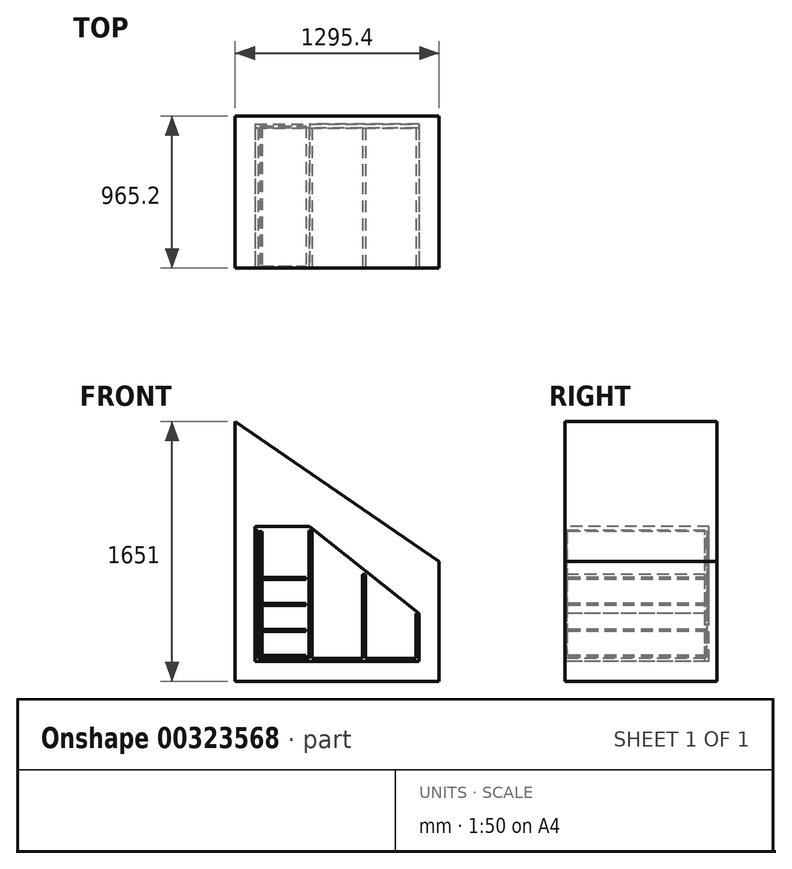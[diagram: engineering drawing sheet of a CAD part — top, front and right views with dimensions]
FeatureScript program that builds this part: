
annotation { "Feature Type Name" : "Feature", "Feature Type Description" : "" }
export const myFeature = defineFeature(function(context is Context, id is Id, definition is map)
    precondition{}
    {
        {
            var Q0;
            Q0=qCreatedBy(makeId("Front.planeOp"),FACE);
            var sketch = newSketch(context, id + "F0", { "sketchPlane" : qUnion([Q0])});
            skLineSegment(sketch, "E0", {"start": v(0, 0) * mm, "end": v(1295.4, 0) * mm});
            skLineSegment(sketch, "E1", {"start": v(1295.4, 0) * mm, "end": v(1295.4, 762) * mm});
            skLineSegment(sketch, "E2", {"start": v(1295.4, 762) * mm, "end": v(0, 1651) * mm});
            skLineSegment(sketch, "E3", {"start": v(0, 1651) * mm, "end": v(0, 0) * mm});
            skSolve(sketch);
        }
        {
            var Q0;
            Q0 = qSketchRegion(id + "F0", true);
            extrude(context, id + "F1", {"entities" : qUnion([Q0]), "depth" : 965.2 * mm});
        }
        {
            var Q0;
            Q0=makeQuery(id+"F1.opExtrude","CAP_FACE",FACE,{"disambiguationData":[OSD([sQuery(id+"F0.wireOp",EDGE,"E0"),sQuery(id+"F0.wireOp",EDGE,"E1"),sQuery(id+"F0.wireOp",EDGE,"E2"),sQuery(id+"F0.wireOp",EDGE,"E3")])],"isStart":false});
            var sketch = newSketch(context, id + "F2", { "sketchPlane" : qUnion([Q0])});
            skLineSegment(sketch, "E4", {"start": v(127, 127) * mm, "end": v(1168.4, 127) * mm});
            skLineSegment(sketch, "E5", {"start": v(1168.4, 127) * mm, "end": v(1168.4, 431.8) * mm});
            skLineSegment(sketch, "E6", {"start": v(1168.4, 431.8) * mm, "end": v(472.95, 985.52) * mm});
            skLineSegment(sketch, "E7", {"start": v(127, 127) * mm, "end": v(127, 985.52) * mm});
            skLineSegment(sketch, "E8", {"start": v(127, 985.52) * mm, "end": v(472.95, 985.52) * mm});
            skSolve(sketch);
        }
        {
            var Q0;
            Q0 = qSketchRegion(id + "F2", true);
            extrude(context, id + "F3", {"entities" : qUnion([Q0]), "operationType" : NewBodyOperationType.REMOVE, "oppositeDirection" : true, "depth" : 914.4 * mm});
        }
        {
            var Q0;
            Q0=makeQuery(id+"F1.opExtrude","CAP_FACE",FACE,{"disambiguationData":[OSD([sQuery(id+"F0.wireOp",EDGE,"E0"),sQuery(id+"F0.wireOp",EDGE,"E1"),sQuery(id+"F0.wireOp",EDGE,"E2"),sQuery(id+"F0.wireOp",EDGE,"E3")])],"isStart":false});
            var sketch = newSketch(context, id + "F4", { "sketchPlane" : qUnion([Q0])});
            skLineSegment(sketch, "E9", {"start": v(127, 127) * mm, "end": v(1168.4, 127) * mm});
            skLineSegment(sketch, "E10", {"start": v(1168.4, 127) * mm, "end": v(1168.4, 431.8) * mm});
            skLineSegment(sketch, "E11", {"start": v(1168.4, 431.8) * mm, "end": v(1149.35, 431.8) * mm});
            skLineSegment(sketch, "E12", {"start": v(1149.35, 431.8) * mm, "end": v(1149.35, 146.05) * mm});
            skLineSegment(sketch, "E13", {"start": v(1149.35, 146.05) * mm, "end": v(827.79, 146.05) * mm});
            skLineSegment(sketch, "E14", {"start": v(146.05, 146.05) * mm, "end": v(146.05, 958.85) * mm});
            skLineSegment(sketch, "E15", {"start": v(146.05, 958.85) * mm, "end": v(127, 958.85) * mm});
            skLineSegment(sketch, "E16", {"start": v(127, 958.85) * mm, "end": v(127, 127) * mm});
            skLineSegment(sketch, "E17.top", {"start": v(467.61, 958.85) * mm, "end": v(486.66, 958.85) * mm});
            skLineSegment(sketch, "E17.left", {"start": v(467.61, 146.05) * mm, "end": v(467.61, 958.85) * mm});
            skLineSegment(sketch, "E17.right", {"start": v(486.66, 146.05) * mm, "end": v(486.66, 958.85) * mm});
            skLineSegment(sketch, "E18.top", {"start": v(808.74, 679.45) * mm, "end": v(827.79, 679.45) * mm});
            skLineSegment(sketch, "E18.left", {"start": v(808.74, 146.05) * mm, "end": v(808.74, 679.45) * mm});
            skLineSegment(sketch, "E18.right", {"start": v(827.79, 146.05) * mm, "end": v(827.79, 679.45) * mm});
            skLineSegment(sketch, "E19.trimOffspring", {"start": v(467.61, 146.05) * mm, "end": v(146.05, 146.05) * mm});
            skLineSegment(sketch, "E20.trimOffspring", {"start": v(808.74, 146.05) * mm, "end": v(486.66, 146.05) * mm});
            skSolve(sketch);
        }
        {
            var Q0;
            Q0 = qSketchRegion(id + "F4", true);
            extrude(context, id + "F5", {"entities" : qUnion([Q0]), "oppositeDirection" : true, "depth" : 889 * mm});
        }
        {
            var Q0;
            Q0=makeQuery(id+"F1.opExtrude","CAP_FACE",FACE,{"disambiguationData":[OSD([sQuery(id+"F0.wireOp",EDGE,"E0"),sQuery(id+"F0.wireOp",EDGE,"E1"),sQuery(id+"F0.wireOp",EDGE,"E2"),sQuery(id+"F0.wireOp",EDGE,"E3")])],"isStart":false});
            cPlane(context, id + "F6", {"entities" : qUnion([Q0]), "cplaneType" : CPlaneType.OFFSET, "offset" : 12.7 * mm, "oppositeDirection" : true, "width" : 152.4 * mm, "height" : 152.4 * mm});
        }
        {
            var Q0;
            Q0=qCreatedBy(id+"F6.planeOp",FACE);
            var sketch = newSketch(context, id + "F7", { "sketchPlane" : qUnion([Q0])});
            skLineSegment(sketch, "E21", {"start": v(158.75, 152.4) * mm, "end": v(450.85, 152.4) * mm});
            skLineSegment(sketch, "E22", {"start": v(158.75, 152.4) * mm, "end": v(158.75, 952.5) * mm});
            skLineSegment(sketch, "E23", {"start": v(158.75, 952.5) * mm, "end": v(171.45, 952.5) * mm});
            skLineSegment(sketch, "E24", {"start": v(171.45, 952.5) * mm, "end": v(171.45, 660.4) * mm});
            skLineSegment(sketch, "E25", {"start": v(171.45, 165.1) * mm, "end": v(450.85, 165.1) * mm});
            skLineSegment(sketch, "E26", {"start": v(450.85, 152.4) * mm, "end": v(450.85, 165.1) * mm});
            skLineSegment(sketch, "E27.bottom", {"start": v(171.45, 330.2) * mm, "end": v(450.85, 330.2) * mm});
            skLineSegment(sketch, "E27.top", {"start": v(171.45, 317.5) * mm, "end": v(450.85, 317.5) * mm});
            skLineSegment(sketch, "E27.right", {"start": v(450.85, 330.2) * mm, "end": v(450.85, 317.5) * mm});
            skLineSegment(sketch, "E28.bottom", {"start": v(171.45, 660.4) * mm, "end": v(450.85, 660.4) * mm});
            skLineSegment(sketch, "E28.top", {"start": v(171.45, 647.7) * mm, "end": v(450.85, 647.7) * mm});
            skLineSegment(sketch, "E28.right", {"start": v(450.85, 660.4) * mm, "end": v(450.85, 647.7) * mm});
            skLineSegment(sketch, "E29.bottom", {"start": v(171.45, 495.3) * mm, "end": v(450.85, 495.3) * mm});
            skLineSegment(sketch, "E29.top", {"start": v(171.45, 482.6) * mm, "end": v(450.85, 482.6) * mm});
            skLineSegment(sketch, "E29.right", {"start": v(450.85, 495.3) * mm, "end": v(450.85, 482.6) * mm});
            skLineSegment(sketch, "E30.trimOffspring", {"start": v(171.45, 647.7) * mm, "end": v(171.45, 495.3) * mm});
            skLineSegment(sketch, "E31.trimOffspring", {"start": v(171.45, 482.6) * mm, "end": v(171.45, 330.2) * mm});
            skLineSegment(sketch, "E32.trimOffspring", {"start": v(171.45, 317.5) * mm, "end": v(171.45, 165.1) * mm});
            skSolve(sketch);
        }
        {
            var Q0;
            Q0 = qSketchRegion(id + "F7", true);
            extrude(context, id + "F8", {"entities" : qUnion([Q0]), "oppositeDirection" : true, "depth" : 889 * mm});
        }
    });
